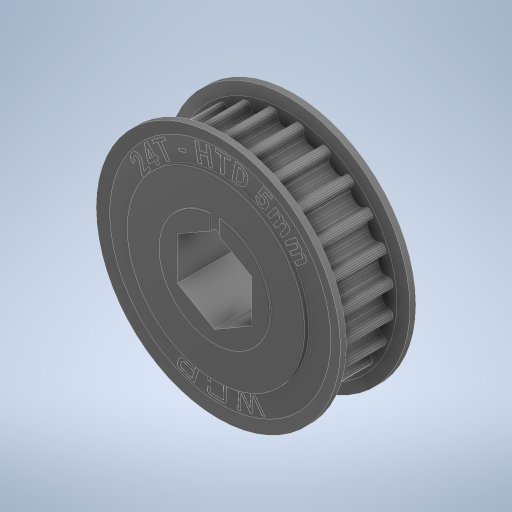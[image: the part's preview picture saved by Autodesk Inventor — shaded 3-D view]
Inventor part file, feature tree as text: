
AUTODESK INVENTOR PART (.ipt)
format: ipt  version: 2024 (Build 280153000, 153)  size: 979,968 bytes
history: native  units: in
note: dims shown in document units (in); Inventor stores cm internally (conversion verified against a paired STEP export)
features: mirror x2, other x1
ambient origin geometry x8: Origin, YZ Plane, XZ Plane, XY Plane, X Axis, Y Axis, Z Axis, Center Point
bodies: Solid1 (feature_tree), Solid2 (feature_tree), Solid3 (feature_tree)
feature tree (3):
  mirror  "Mirror2"
  mirror  "Mirror1"
  other  "Cut-Extrude5"
